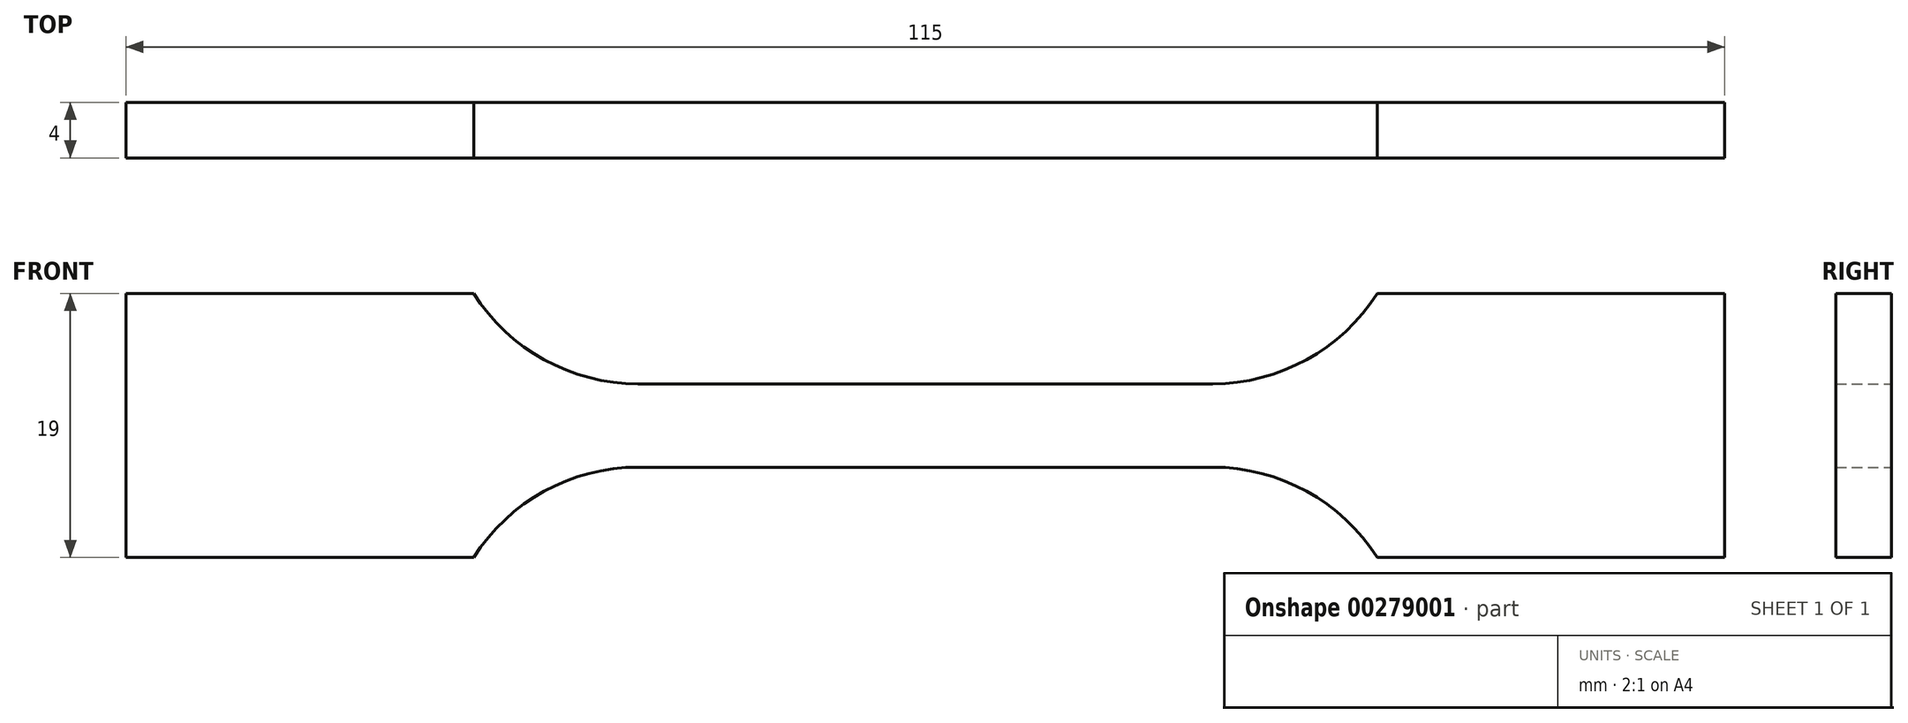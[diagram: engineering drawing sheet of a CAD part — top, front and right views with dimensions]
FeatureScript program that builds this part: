
annotation { "Feature Type Name" : "Feature", "Feature Type Description" : "" }
export const myFeature = defineFeature(function(context is Context, id is Id, definition is map)
    precondition{}
    {
        {
            var Q0;
            Q0=qCreatedBy(makeId("Front.planeOp"),FACE);
            var sketch = newSketch(context, id + "F0", { "sketchPlane" : qUnion([Q0])});
            skLineSegment(sketch, "E0", {"start": v(0, 3) * mm, "end": v(20.68, 3) * mm});
            skArc(sketch, "E1", {"start": v(20.68, 3) * mm, "mid": v(27.42, 4.73) * mm, "end": v(32.5, 9.5) * mm});
            skLineSegment(sketch, "E2", {"start": v(32.5, 9.5) * mm, "end": v(57.5, 9.5) * mm});
            skLineSegment(sketch, "E3.MirrorCS", {"start": v(32.5, -9.5) * mm, "end": v(57.5, -9.5) * mm});
            skLineSegment(sketch, "E4.MirrorCS", {"start": v(0, -3) * mm, "end": v(20.68, -3) * mm});
            skArc(sketch, "E5.MirrorCS", {"start": v(20.68, -3) * mm, "mid": v(27.42, -4.73) * mm, "end": v(32.5, -9.5) * mm});
            skArc(sketch, "E6.MirrorCS", {"start": v(-20.68, -3) * mm, "mid": v(-27.42, -4.73) * mm, "end": v(-32.5, -9.5) * mm});
            skLineSegment(sketch, "E7.MirrorCS", {"start": v(0, 3) * mm, "end": v(-20.68, 3) * mm});
            skArc(sketch, "E8.MirrorCS", {"start": v(-20.68, 3) * mm, "mid": v(-27.42, 4.73) * mm, "end": v(-32.5, 9.5) * mm});
            skLineSegment(sketch, "E9.MirrorCS", {"start": v(-32.5, -9.5) * mm, "end": v(-57.5, -9.5) * mm});
            skLineSegment(sketch, "E10.MirrorCS", {"start": v(0, -3) * mm, "end": v(-20.68, -3) * mm});
            skLineSegment(sketch, "E11.MirrorCS", {"start": v(-32.5, 9.5) * mm, "end": v(-57.5, 9.5) * mm});
            skLineSegment(sketch, "E12", {"start": v(-57.5, 9.5) * mm, "end": v(-57.5, -9.5) * mm});
            skLineSegment(sketch, "E13", {"start": v(57.5, 9.5) * mm, "end": v(57.5, -9.5) * mm});
            skSolve(sketch);
        }
        {
            var Q0;
            Q0=makeQuery(id+"F0.imprint","IMPRINT",FACE,{"disambiguationData":[TD([[makeQuery(id+"F0.imprint","IMPRINT",EDGE,{"derivedFrom":sQuery(id+"F0.wireOp",EDGE,"E0")}),-1.0]])]});
            extrude(context, id + "F1", {"entities" : qUnion([Q0]), "endBound" : BoundingType.SYMMETRIC, "depth" : 4 * mm});
        }
    });
